# Revit family: Door-Curtain_Wall-Wicona-Wicstyle_75_Evo
name_source: partatom
category: Doors
revit_build: Autodesk Revit Architecture 2014 (Build: 20130308_1515(x64)
units: mm (PartAtom-declared; Revit-internal decimal feet)

## types (2) — shared parameters
Acoustic Performance = Rw (C; Ctr) until 43 (-2; -5) dB
Air Permeability = Until Class 4
Analytic Construction = <None>
Behaviour between different climates = Until Class 2(e) 2(d)
Burglar Resistance = RC1N, RC2N, RC2, RC3, SBD
Date of publishing = 2015-03-14
Description = With 75 mm profile depth, WICSTYLE 75 evo puts itself ahead in terms of thermal insulation and physical features. Its outstanding technical performance and application range make it the ideal door solution for all current and future requirements in architecture, both in new buildings and in renovations.
Design country = Germany
Edition number = 1
Frame Material = WICONA - Aluminium - RAL7016 - Anthracite Grey - Matt
Front Offset from Centre = 19 mm  [stored 0.062336 ft]
Head Offset = 20 mm  [stored 0.0656168 ft]
Impact Resistance = Class 1
Jamb Offset = 20 mm  [stored 0.0656168 ft]
Keynote = L20
Load Bearing Capacity of Safety Devices = Fulfilled
Manufacturer = Wicona
Manufacturer country = Germany
Manufacturer name = Wicona
Material main = Aluminium
Material secondary = Glass
Mechanical Strength = Class 3
Model = WICSTYLE 75 evo
Nominal height = 252000
Nominal width = 120000
Operating Forces = Class 2
Product Guid = 64f1b286-9f1b-4a78-aa41-f2a8b267cce1
Product SKU = WICSTYLE_75_EVO_D
Product data url = http://bimobject.com
Product family = Windows & Doors
Product group = Windows
QR code = http://bimobject.com
Quality Assurance = Creadited according to ISO 9001:2008
Repeated Opening/Closing = Until class 7 (500,000 cycles)
Resistance to wind load = Class C2
Thickness = 75 mm
Threshold Material = WICONA - Anodised Aluminium - AA25 - Natural Silver
URL = http://www.wicona.co.uk
Watertightness = Until 7A
zero-valued in all types: Conection IN Dia, Threshold Offset, Weight Net (Kg)

## per-type parameters (varying)
| type | Assembly Code | Function | Handle Height | Operation |
| Double Door | B2030110 | Interior | 932.5 mm | IFC_DOORDBLSWING |
| Single Door |  | Exterior | 900 mm | IFC_DOORSGLSWING |

note: column(s) folded — value = type name in every type: Type Comments

type visibility flags (boolean, named after types; folded from table):
- Double Door: Yes: Double Door
- Single Door: Yes: (none)

note: [stored X ft] marks values corroborated as IEEE doubles in the binary element streams (Revit-internal decimal feet)

## geometry (parser evidence)
native form markers: Blend x6, Sweep x9
no freeform markers — native parametric forms only
